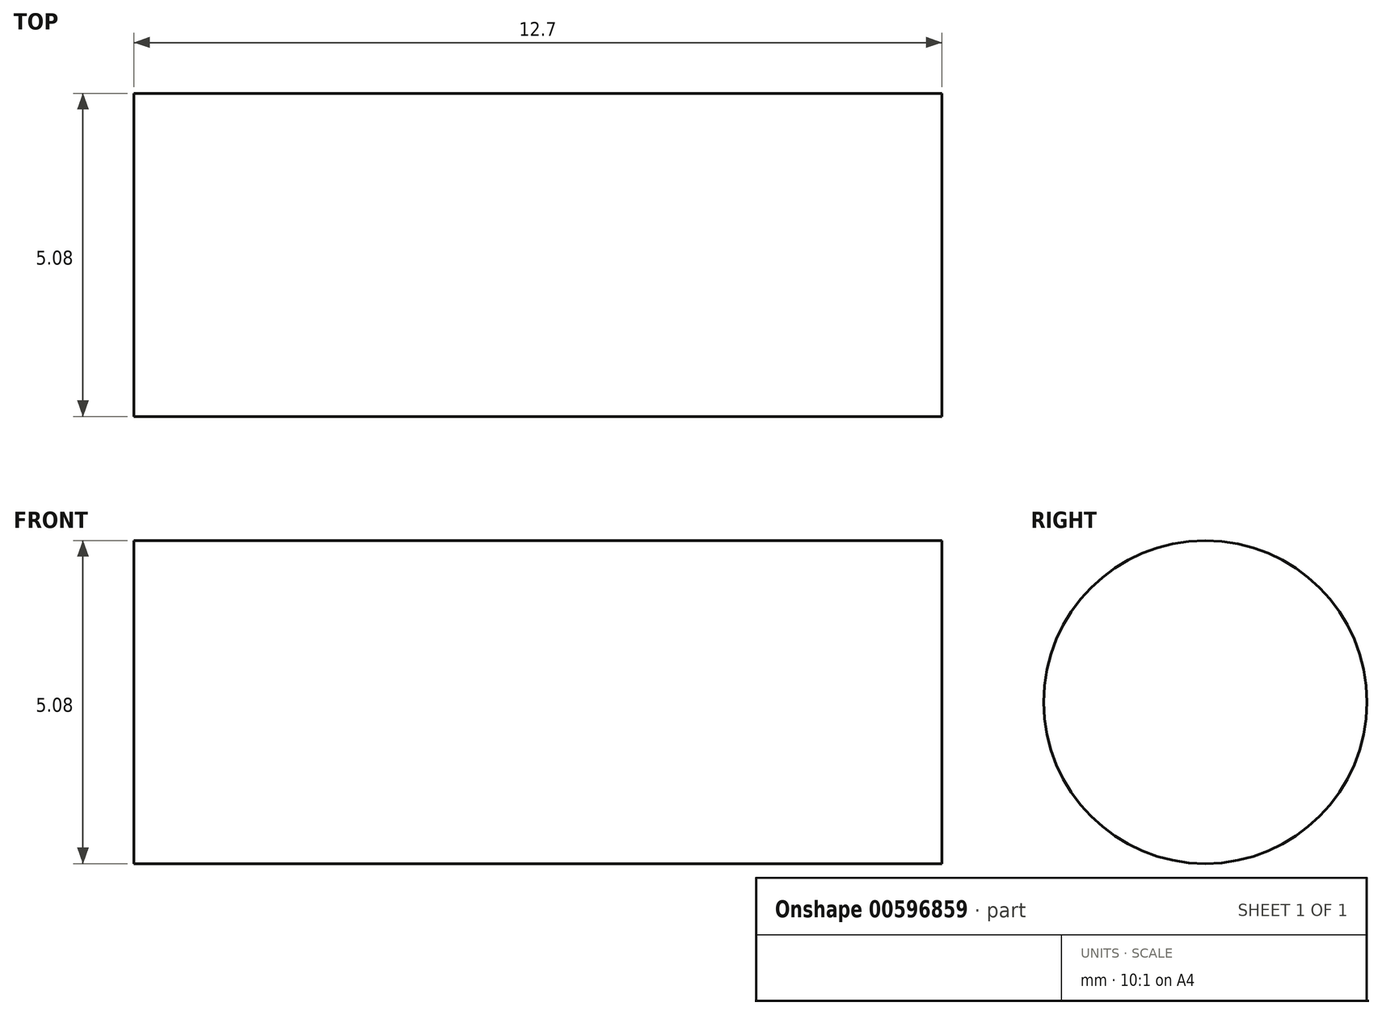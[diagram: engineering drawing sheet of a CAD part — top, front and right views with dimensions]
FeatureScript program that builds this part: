
annotation { "Feature Type Name" : "Feature", "Feature Type Description" : "" }
export const myFeature = defineFeature(function(context is Context, id is Id, definition is map)
    precondition{}
    {
        {
            var Q0;
            Q0=qCreatedBy(makeId("Right.planeOp"),FACE);
            var sketch = newSketch(context, id + "F0", { "sketchPlane" : qUnion([Q0])});
            skCircle(sketch, "E0", {"center": v(0, 0) * mm, "radius": 38.1 * mm});
            skSolve(sketch);
        }
        {
            var Q0;
            Q0 = qSketchRegion(id + "F0", true);
            extrude(context, id + "F1", {"entities" : qUnion([Q0]), "depth" : 25.4 * mm, "offsetDistance" : 25.4 * mm});
        }
        {
            var Q0;
            Q0 = qSketchRegion(id + "F0", true);
            extrude(context, id + "F2", {"entities" : qUnion([Q0]), "depth" : 25.4 * mm, "offsetDistance" : 25.4 * mm});
        }
        {
            var Q0;
            Q0=makeQuery(id+"F1.opExtrude","CAP_FACE",FACE,{"disambiguationData":[OSD([sQuery(id+"F0.wireOp",EDGE,"E0")])],"isStart":false});
            var sketch = newSketch(context, id + "F3", { "sketchPlane" : qUnion([Q0])});
            skLineSegment(sketch, "E1.bottom", {"start": v(-9.52, 50.8) * mm, "end": v(9.53, 50.8) * mm});
            skLineSegment(sketch, "E1.top", {"start": v(-9.52, 25.4) * mm, "end": v(9.53, 25.4) * mm});
            skLineSegment(sketch, "E1.left", {"start": v(-9.52, 50.8) * mm, "end": v(-9.52, 25.4) * mm});
            skLineSegment(sketch, "E1.right", {"start": v(9.53, 50.8) * mm, "end": v(9.53, 25.4) * mm});
            skPoint(sketch, "E1.middle", {"position": v(0, 38.1) * mm});
            skSolve(sketch);
        }
        {
            var Q0;
            Q0 = qSketchRegion(id + "F3", true);
            extrude(context, id + "F4", {"entities" : qUnion([Q0]), "oppositeDirection" : true, "depth" : 25.4 * mm, "offsetDistance" : 25.4 * mm});
        }
        {
            var Q0;
            Q0=makeQuery(id+"F4.opExtrude","SWEPT_EDGE",EDGE,{"disambiguationData":[OSD([sQuery(id+"F3.wireOp",EDGE,"E1.bottom"),sQuery(id+"F3.wireOp",EDGE,"E1.left")])]});
            var Q1;
            Q1=makeQuery(id+"F4.opExtrude","SWEPT_EDGE",EDGE,{"disambiguationData":[OSD([sQuery(id+"F3.wireOp",EDGE,"E1.bottom"),sQuery(id+"F3.wireOp",EDGE,"E1.right")])]});
            fillet(context, id + "F5", {"entities" : qUnion([Q0, Q1]), "radius" : 5.08 * mm, "tangentPropagation" : true, "allowEdgeOverflow" : false});
        }
        {
            var Q0;
            Q0=makeQuery(id+"F4.opExtrude","SWEPT_BODY",BODY,{"disambiguationData":[OSD([sQuery(id+"F3.wireOp",EDGE,"E1.bottom"),sQuery(id+"F3.wireOp",EDGE,"E1.top"),sQuery(id+"F3.wireOp",EDGE,"E1.left"),sQuery(id+"F3.wireOp",EDGE,"E1.right")])]});
            var Q1;
            Q1=makeQuery(id+"F1.opExtrude","CAP_EDGE",EDGE,{"disambiguationData":[OSD([sQuery(id+"F0.wireOp",EDGE,"E0")])],"isStart":false});
            circularPattern(context, id + "F6", {"entities" : qUnion([Q0]), "axis" : qUnion([Q1]), "angle" : 360 * degree, "instanceCount" : 5, "equalSpace" : true});
        }
        {
            var Q0;
            Q0=makeQuery(id+"F1.opExtrude","CAP_FACE",FACE,{"disambiguationData":[OSD([sQuery(id+"F0.wireOp",EDGE,"E0")])],"isStart":false});
            var sketch = newSketch(context, id + "F7", { "sketchPlane" : qUnion([Q0])});
            skLineSegment(sketch, "E2", {"start": v(0, 189.13) * mm, "end": v(-127, 189.13) * mm});
            skLineSegment(sketch, "E3", {"start": v(-22.97, 30.4) * mm, "end": v(0, 0) * mm});
            skLineSegment(sketch, "E4", {"start": v(0, 0) * mm, "end": v(21.99, 31.12) * mm});
            skLineSegment(sketch, "E5", {"start": v(0, 0) * mm, "end": v(0, -38.1) * mm});
            skLineSegment(sketch, "E6", {"start": v(0, 0) * mm, "end": v(36.85, -9.66) * mm});
            skLineSegment(sketch, "E7", {"start": v(0, 0) * mm, "end": v(-36.82, -9.79) * mm});
            skCircle(sketch, "E8", {"center": v(-22.97, 30.4) * mm, "radius": 6.35 * mm});
            skCircle(sketch, "E9", {"center": v(-22.97, 30.4) * mm, "radius": 6.33 * mm});
            skSolve(sketch);
        }
        {
            var Q0;
            Q0=makeQuery(id+"F1.opExtrude","CAP_FACE",FACE,{"disambiguationData":[OSD([sQuery(id+"F0.wireOp",EDGE,"E0")])],"isStart":true});
            var sketch = newSketch(context, id + "F8", { "sketchPlane" : qUnion([Q0])});
            skCircle(sketch, "E10", {"center": v(0, 0) * mm, "radius": 12.7 * mm});
            skCircle(sketch, "E11", {"center": v(0, 0) * mm, "radius": 2.54 * mm});
            skSolve(sketch);
        }
        {
            var Q0;
            Q0 = qSketchRegion(id + "F8", true);
            extrude(context, id + "F9", {"entities" : qUnion([Q0]), "depth" : 25.4 * mm, "offsetDistance" : 25.4 * mm});
        }
        {
            var Q0;
            Q0=makeQuery(id+"F9.opExtrude","CAP_EDGE",EDGE,{"disambiguationData":[OSD([sQuery(id+"F8.wireOp",EDGE,"E10")])],"isStart":false});
            chamfer(context, id + "F10", {"entities" : qUnion([Q0]), "width" : 5.08 * mm, "tangentPropagation" : true});
        }
        {
            var Q0;
            Q0=makeQuery(id+"F1.opExtrude","CAP_FACE",FACE,{"disambiguationData":[OSD([sQuery(id+"F0.wireOp",EDGE,"E0")])],"isStart":true});
            var sketch = newSketch(context, id + "F11", { "sketchPlane" : qUnion([Q0])});
            skCircle(sketch, "E12", {"center": v(0, 0) * mm, "radius": 2.54 * mm});
            skSolve(sketch);
        }
        {
            var Q0;
            Q0 = qSketchRegion(id + "F11", true);
            extrude(context, id + "F12", {"entities" : qUnion([Q0]), "operationType" : NewBodyOperationType.INTERSECT, "oppositeDirection" : true, "depth" : 12.7 * mm, "offsetDistance" : 25.4 * mm});
        }
        {
            var Q0;
            {var subQ0=sQuery(id+"F7.wireOp",EDGE,"E3");var subQ1=makeQuery(id+"F1.opExtrude","CAP_EDGE",EDGE,{"disambiguationData":[OSD([sQuery(id+"F0.wireOp",EDGE,"E0")])],"isStart":false});var subQ2=makeQuery(id+"F7.imprint","INTERSECT",VERTEX,{"derivedFrom":[subQ1,subQ0]});Q0=makeQuery(id+"F7.imprint","IMPRINT",FACE,{"disambiguationData":[TD([[makeQuery(id+"F7.imprint","IMPRINT",EDGE,{"disambiguationData":[TD([[subQ2,-1.0]])],"derivedFrom":subQ0}),-1.0]])]});}
            var sketch = newSketch(context, id + "F13", { "sketchPlane" : qUnion([Q0])});
            skCircle(sketch, "E13", {"center": v(-22.94, 30.46) * mm, "radius": 7.62 * mm});
            skSolve(sketch);
        }
        {
            var Q0;
            Q0 = qSketchRegion(id + "F13", true);
            extrude(context, id + "F14", {"entities" : qUnion([Q0]), "operationType" : NewBodyOperationType.REMOVE, "endBound" : BoundingType.THROUGH_ALL, "oppositeDirection" : true, "depth" : 25.4 * mm, "offsetDistance" : 25.4 * mm});
        }
        {
            var Q0;
            {var subQ0=sQuery(id+"F7.wireOp",EDGE,"E4");Q0=makeQuery(id+"F7.imprint","IMPRINT",FACE,{"disambiguationData":[TD([[makeQuery(id+"F7.imprint","IMPRINT",EDGE,{"derivedFrom":subQ0}),-1.0]])]});}
            var sketch = newSketch(context, id + "F15", { "sketchPlane" : qUnion([Q0])});
            skCircle(sketch, "E14", {"center": v(21.97, 31.06) * mm, "radius": 7.62 * mm});
            skSolve(sketch);
        }
        {
            var Q0;
            Q0 = qSketchRegion(id + "F15", true);
            extrude(context, id + "F16", {"entities" : qUnion([Q0]), "operationType" : NewBodyOperationType.REMOVE, "endBound" : BoundingType.THROUGH_ALL, "oppositeDirection" : true, "depth" : 25.4 * mm, "offsetDistance" : 25.4 * mm});
        }
        {
            var Q0;
            {var subQ0=sQuery(id+"F7.wireOp",EDGE,"E4");Q0=makeQuery(id+"F7.imprint","IMPRINT",FACE,{"disambiguationData":[TD([[makeQuery(id+"F7.imprint","IMPRINT",EDGE,{"derivedFrom":subQ0}),-1.0]])]});}
            var sketch = newSketch(context, id + "F17", { "sketchPlane" : qUnion([Q0])});
            skCircle(sketch, "E15", {"center": v(36.86, -9.65) * mm, "radius": 7.62 * mm});
            skSolve(sketch);
        }
        {
            var Q0;
            Q0 = qSketchRegion(id + "F17", true);
            extrude(context, id + "F18", {"entities" : qUnion([Q0]), "operationType" : NewBodyOperationType.REMOVE, "endBound" : BoundingType.THROUGH_ALL, "oppositeDirection" : true, "depth" : 25.4 * mm, "offsetDistance" : 25.4 * mm});
        }
        {
            var Q0;
            {var subQ0=sQuery(id+"F7.wireOp",EDGE,"E5");Q0=makeQuery(id+"F7.imprint","IMPRINT",FACE,{"disambiguationData":[TD([[makeQuery(id+"F7.imprint","IMPRINT",EDGE,{"derivedFrom":subQ0}),1.0]])]});}
            var sketch = newSketch(context, id + "F19", { "sketchPlane" : qUnion([Q0])});
            skCircle(sketch, "E16", {"center": v(0, -52.99) * mm, "radius": 7.62 * mm});
            skCircle(sketch, "E17", {"center": v(0, -38.09) * mm, "radius": 7.62 * mm});
            skSolve(sketch);
        }
        {
            var Q0;
            Q0 = qSketchRegion(id + "F19", true);
            extrude(context, id + "F20", {"entities" : qUnion([Q0]), "operationType" : NewBodyOperationType.REMOVE, "endBound" : BoundingType.THROUGH_ALL, "oppositeDirection" : true, "depth" : 25.4 * mm, "offsetDistance" : 25.4 * mm});
        }
        {
            var Q0;
            {var subQ0=sQuery(id+"F7.wireOp",EDGE,"E5");Q0=makeQuery(id+"F7.imprint","IMPRINT",FACE,{"disambiguationData":[TD([[makeQuery(id+"F7.imprint","IMPRINT",EDGE,{"derivedFrom":subQ0}),1.0]])]});}
            var sketch = newSketch(context, id + "F21", { "sketchPlane" : qUnion([Q0])});
            skCircle(sketch, "E18", {"center": v(-36.76, -9.73) * mm, "radius": 7.62 * mm});
            skSolve(sketch);
        }
        {
            var Q0;
            Q0 = qSketchRegion(id + "F21", true);
            extrude(context, id + "F22", {"entities" : qUnion([Q0]), "operationType" : NewBodyOperationType.REMOVE, "endBound" : BoundingType.THROUGH_ALL, "oppositeDirection" : true, "depth" : 25.4 * mm, "offsetDistance" : 25.4 * mm});
        }
    });
